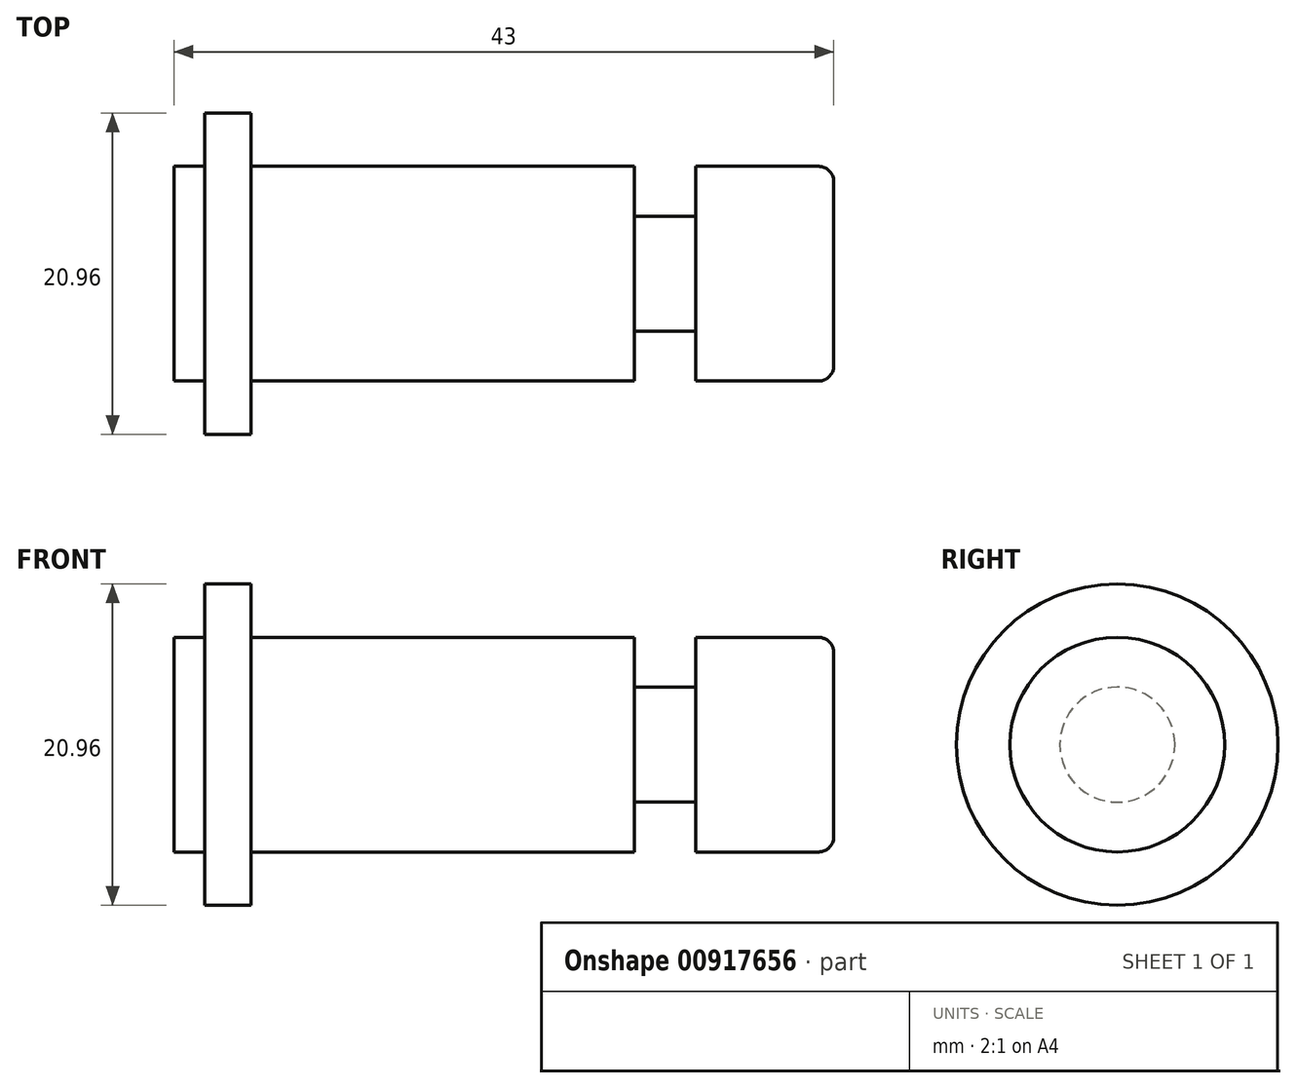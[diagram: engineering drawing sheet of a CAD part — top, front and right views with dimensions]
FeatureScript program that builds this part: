
annotation { "Feature Type Name" : "Feature", "Feature Type Description" : "" }
export const myFeature = defineFeature(function(context is Context, id is Id, definition is map)
    precondition{}
    {
        {
            var Q0;
            Q0=qCreatedBy(makeId("Front.planeOp"),FACE);
            var sketch = newSketch(context, id + "F0", { "sketchPlane" : qUnion([Q0])});
            skLineSegment(sketch, "E0", {"start": v(0, 0) * mm, "end": v(0, 7) * mm});
            skLineSegment(sketch, "E1", {"start": v(0, 7) * mm, "end": v(2, 7) * mm});
            skLineSegment(sketch, "E2", {"start": v(2, 7) * mm, "end": v(2, 10.48) * mm});
            skLineSegment(sketch, "E3", {"start": v(2, 10.48) * mm, "end": v(5, 10.48) * mm});
            skLineSegment(sketch, "E4", {"start": v(5, 10.48) * mm, "end": v(5, 7) * mm});
            skLineSegment(sketch, "E5", {"start": v(5, 7) * mm, "end": v(30, 7) * mm});
            skLineSegment(sketch, "E6", {"start": v(30, 7) * mm, "end": v(30, 3.75) * mm});
            skLineSegment(sketch, "E7", {"start": v(30, 3.75) * mm, "end": v(34, 3.75) * mm});
            skLineSegment(sketch, "E8", {"start": v(0, 0) * mm, "end": v(43, 0) * mm});
            skLineSegment(sketch, "E9", {"start": v(43, 0) * mm, "end": v(43, 7) * mm});
            skLineSegment(sketch, "E10", {"start": v(43, 7) * mm, "end": v(34, 7) * mm});
            skLineSegment(sketch, "E11", {"start": v(34, 7) * mm, "end": v(34, 3.75) * mm});
            skSolve(sketch);
        }
        {
            var Q0;
            Q0 = qSketchRegion(id + "F0", true);
            var Q1;
            Q1=sQuery(id+"F0.wireOp",EDGE,"E8");
            revolve(context, id + "F1", {"surfaceOperationType" : NewSurfaceOperationType.NEW, "entities" : qUnion([Q0]), "axis" : qUnion([Q1]), "revolveType" : RevolveType.FULL});
        }
        {
            var Q0;
            Q0=makeQuery(id+"F1.opRevolve","SWEPT_EDGE",EDGE,{"disambiguationData":[OSD([sQuery(id+"F0.wireOp",EDGE,"E9"),sQuery(id+"F0.wireOp",EDGE,"E10")])]});
            fillet(context, id + "F2", {"entities" : qUnion([Q0]), "radius" : 1 * mm, "tangentPropagation" : true, "allowEdgeOverflow" : false});
        }
    });
